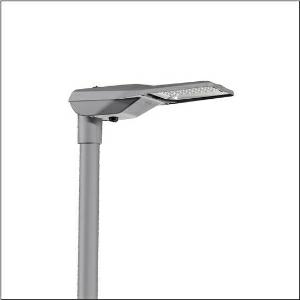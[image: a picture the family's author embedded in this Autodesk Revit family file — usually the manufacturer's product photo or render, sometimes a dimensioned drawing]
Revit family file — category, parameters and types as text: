
# Revit family: streetlight_sl_21_mini___stw1_0a_5xe2e23t08hb_3503
name_source: partatom
category: Lighting Fixtures
units: mm (PartAtom-declared; Revit-internal decimal feet)

## family parameters
Cut with Voids When Loaded = No
Host = Face
Light Source = No
Part Type = Normal
Room Calculation Point = No
Round Connector Dimension = Use Diameter
Shared = No

## types (1)
- --- (1 x LED, 7490 lm, 66 W, 2200K)
    Apparent Load = 66 VA
    CIE Flux Codes = 38 75 98 100 100
    Color Rendering = 70
    Color Temperature = 2200K
    Default Elevation = 1800 mm
    Description = Streetlight SL 21 mini, mast luminaire, primary light control with lens, of PMMA, primary optical cover: cover, of toughened safety glass, transparent, light distribution: STW1.0a, light emission: direct distribution, primary light characteristic: asymmetric, installation type: side-entry, post-top, LED, High Power LED, rated luminous flux: 7.490lm, luminous efficacy: 114lm/W, light colour: 722, colour temperature: 2200K, control gear: D4i, control: overheat protection, constant luminous flux control, time-dependent luminous flux control, flexible luminous flux parameterisation, pre-setting: logarithmic dimming characteristic, mains connection: 220..240V, AC, 50/60Hz, start of lifetime: 66W, end of service life: 69W, reduction: 30W, luminaire housing, of diecast aluminium, powder-coated, Siteco® metallic grey (DB 702S), corrosivity category C5 mid according to DIN EN ISO 12944, please order mast flange separately, inclination adjustable: 0°, 5°, 10°, 15°, sealing non-destructively replaceable, multi-level sealing system, length: 628mm, width: 235mm, height: 110mm, mast flange for spigot size: 42mm (side-entry): 5XC10008XM4, 60/48mm (side-entry/post-top): 5XC10108XM2, 76/60mm (side-entry/post-top): 5XC10108XM1, mounting height: 4..8m, Smart Interface below and above, protection rating (complete): IP66, insulation class (complete): insulation class II (safety insulation), certification: CE, ENEC, ENEC+, VDE, impact resistance: IK10, permissible operating ambient temperature for outdoor applications: -40..+50°C, standard-compliant lighting for roads and squares, packaging unit: 1 piece

Light Distribution: STW1.0a
    Height = 110 mm
    Lamp = 1 x LED
    Lamp Light Flux = 7490 lm
    Lamp Power = 66 W
    Lamp count = 1
    Length = 625 mm
    Luminous efficacy = 113 lm/W
    Manufacturer = Siteco
    ModVariant = No
    Model = 5XE2E23T08HB
    Number of Poles = 1
    OnlyDefault = Yes
    Power Factor = 1
    Product Name = Streetlight SL 21 mini | STW1.0a
    Product group = mast luminaire | pylon top
    ProductGroupID = 6100
    Protection Class = Protection class II
    Protection Degree = IP 66
    RLX_Detail_Level = 1
    RLX_Emergency_Light_Flux = 0 lm
    RLX_Emergency_Type = 0
    RLX_Emergency_Type_DB = No
    RlxData = <blob elided: 26321 chars, md5=2006da7a>
    Socket = socket
    Standby Power = 0 W
    System Light Flux = 7490 lm
    System Power = 66 W
    Type Comments = factory setting: luminous flux: 100 % | dim-lin: 254 | 670 mA
    Type Image = l_1003514.jpg
    URL = http://relux.com
    VarID = @adj_187222
    Voltage = 0 V
    Weight = 0.00 kg
    Width = 234 mm

## geometry (parser evidence)
native form markers: Blend x4, Sweep x11
no freeform markers — native parametric forms only
